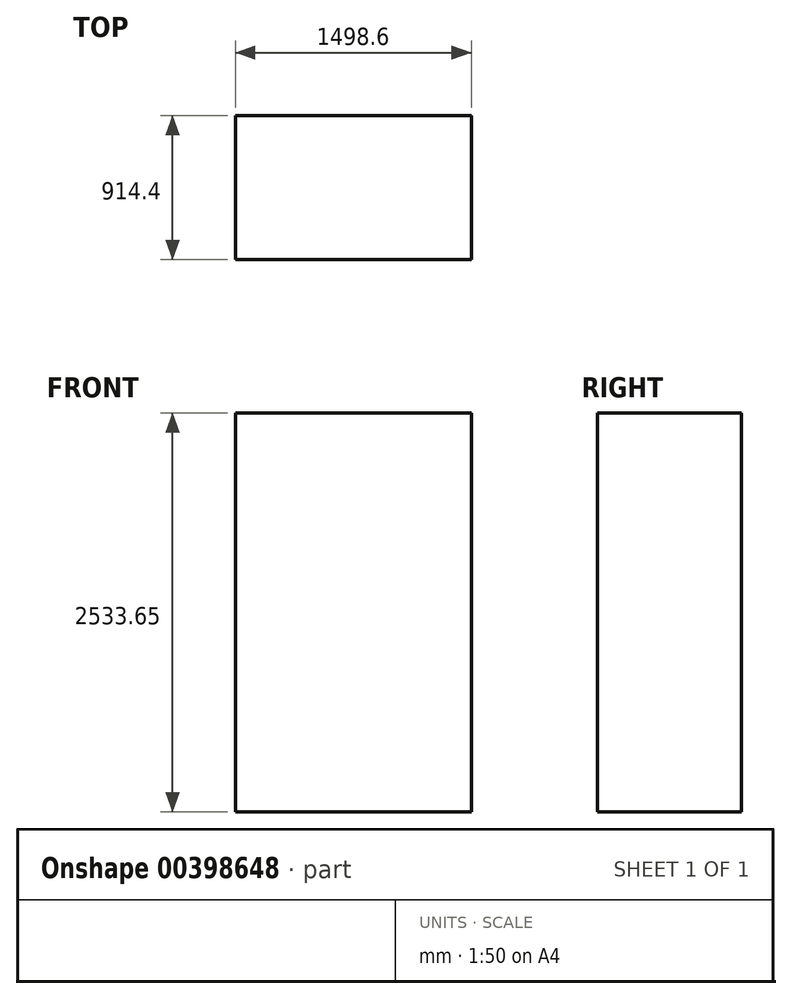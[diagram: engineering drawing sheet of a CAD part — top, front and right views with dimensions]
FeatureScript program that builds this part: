
annotation { "Feature Type Name" : "Feature", "Feature Type Description" : "" }
export const myFeature = defineFeature(function(context is Context, id is Id, definition is map)
    precondition{}
    {
        {
            var Q0;
            Q0=qCreatedBy(makeId("Top.planeOp"),FACE);
            var sketch = newSketch(context, id + "F0", { "sketchPlane" : qUnion([Q0])});
            skLineSegment(sketch, "E0", {"start": v(0, 0) * mm, "end": v(-1498.6, 0) * mm});
            skLineSegment(sketch, "E1", {"start": v(0, 0) * mm, "end": v(0, -914.4) * mm});
            skLineSegment(sketch, "E2", {"start": v(0, -914.4) * mm, "end": v(-1498.6, -914.4) * mm});
            skLineSegment(sketch, "E3", {"start": v(-1498.6, -914.4) * mm, "end": v(-1498.6, 0) * mm});
            skSolve(sketch);
        }
        {
            var Q0;
            Q0 = qSketchRegion(id + "F0", true);
            extrude(context, id + "F1", {"entities" : qUnion([Q0]), "depth" : 2533.65 * mm});
        }
    });
